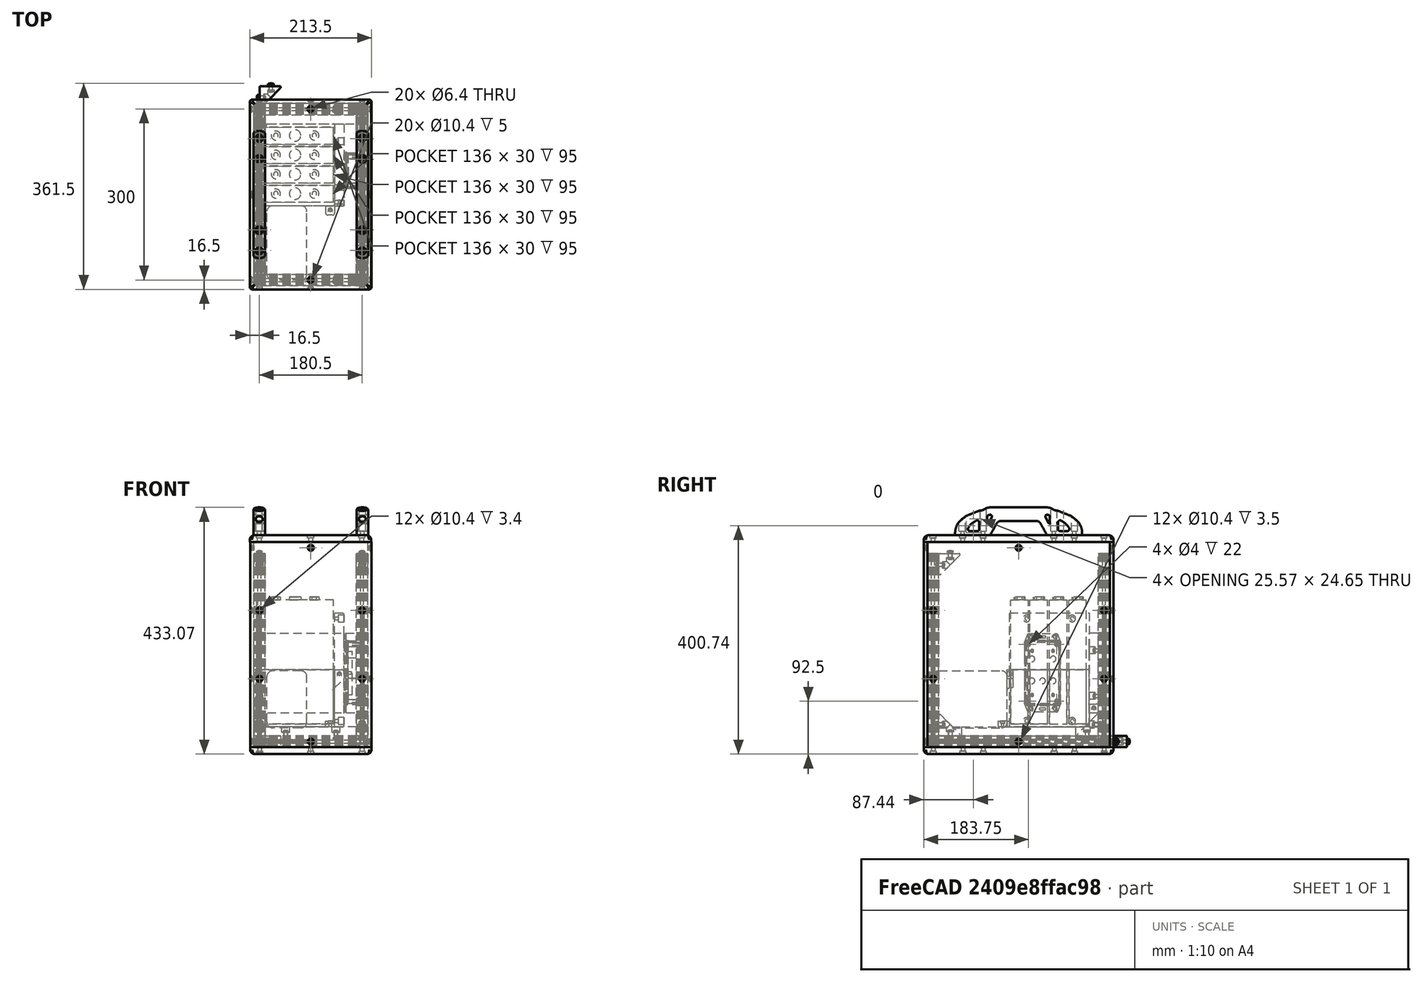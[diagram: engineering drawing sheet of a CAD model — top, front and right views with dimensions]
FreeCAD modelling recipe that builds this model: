
FCSTD DOCUMENT  (FreeCAD 0.17R9796 (Git))
Label: UPKframeNG2g
License: All rights reserved
LicenseURL: http://en.wikipedia.org/wiki/All_rights_reserved
objects: Part::Feature×72, Part::FeaturePython×24, Part::Compound×12, App::FeaturePython×8, App::Part×6, Part::Cylinder×5, Part::Box×4, Part::Cut×4, PartDesign::Body×2, PartDesign::Pocket×1, Part::Fillet×1, Part::MultiFuse×1
note: 127 computed .brp shape members not serialized (recipe doc carries the construction recipe); baked Part::Feature solids carry a one-line shape summary decoded from their .brp

FEATURE [Part::Feature] Pocket003001  label="tslot32con"
  Placement = pos=(0,10,10) rot=(1,0,0;1.5708rad)
  shape: bbox 20 x 320 x 20 mm, 150 faces (baked)
FEATURE [Part::Feature] Pocket003002  label="tslot16"
  Placement = pos=(10,0,10) rot=(0,1,0;1.5708rad)
  shape: bbox 160 x 20 x 20 mm, 94 faces (baked)
FEATURE [Part::Feature] Pocket003006  label="tslot16_001"
  Placement = pos=(10,-300,10) rot=(0,1,0;1.5708rad)
  shape: bbox 160 x 20 x 20 mm, 94 faces (baked)
FEATURE [Part::Feature] Pocket003007  label="tslot32con_001"
  Placement = pos=(180,-310,10) rot=(0,0.707107,0.707107;3.14159rad)
  shape: bbox 20 x 320 x 20 mm, 150 faces (baked)
FEATURE [Part::FeaturePython] Screw  label="M6x25-Screw"  # Fasteners workbench fastener (typed FeaturePython)
  Placement = pos=(-4,0,10) rot=(0,-1,0;1.5708rad)
  diameter = 7
  invert = false
  length = 6
  matchOuter = false
  offset = 0
  thread = false
  type = 15
FEATURE [Part::FeaturePython] Screw001  label="M6x25-Screw004"  # Fasteners workbench fastener (typed FeaturePython)
  Placement = pos=(-4,-300,10) rot=(0,-1,0;1.5708rad)
  diameter = 7
  invert = false
  length = 6
  matchOuter = false
  offset = 0
  thread = false
  type = 15
FEATURE [Part::FeaturePython] Screw002  label="M6x25-Screw005"  # Fasteners workbench fastener (typed FeaturePython)
  Placement = pos=(184,0,10) rot=(0,1,0;1.5708rad)
  diameter = 7
  invert = false
  length = 6
  matchOuter = false
  offset = 0
  thread = false
  type = 15
FEATURE [Part::FeaturePython] Screw004  label="M6x25-Screw006"  # Fasteners workbench fastener (typed FeaturePython)
  Placement = pos=(184,-300,10) rot=(0,1,0;1.5708rad)
  diameter = 7
  invert = false
  length = 6
  matchOuter = false
  offset = 0
  thread = false
  type = 15
FEATURE [App::Part] Part  label="lower_frame"
  Group = -> [Pocket003001,Pocket003002,Pocket003006,Pocket003007,Screw,Screw001,Screw002,Screw004]
  License = CC BY 3.0
  LicenseURL = http://creativecommons.org/licenses/by/3.0/
  Origin = -> PartOrigin
FEATURE [Part::Feature] Pocket003008  label="tslot32con001"
  Placement = pos=(0,10,10) rot=(1,0,0;1.5708rad)
  shape: bbox 20 x 320 x 20 mm, 150 faces (baked)
FEATURE [Part::Feature] Pocket003009  label="tslot041"
  Placement = pos=(10,0,10) rot=(0,1,0;1.5708rad)
  shape: bbox 160 x 20 x 20 mm, 94 faces (baked)
FEATURE [Part::Feature] Pocket003010  label="tslot16_002"
  Placement = pos=(10,-300,10) rot=(0,1,0;1.5708rad)
  shape: bbox 160 x 20 x 20 mm, 94 faces (baked)
FEATURE [Part::Feature] Pocket003011  label="tslot32con_002"
  Placement = pos=(180,-310,10) rot=(0,0.707107,0.707107;3.14159rad)
  shape: bbox 20 x 320 x 20 mm, 150 faces (baked)
FEATURE [Part::FeaturePython] Screw005  label="M6x25-Screw007"  # Fasteners workbench fastener (typed FeaturePython)
  Placement = pos=(-4,0,10) rot=(0,-1,0;1.5708rad)
  diameter = 7
  invert = false
  length = 6
  matchOuter = false
  offset = 0
  thread = false
  type = 15
FEATURE [Part::FeaturePython] Screw006  label="M6x25-Screw008"  # Fasteners workbench fastener (typed FeaturePython)
  Placement = pos=(-4,-300,10) rot=(0,-1,0;1.5708rad)
  diameter = 7
  invert = false
  length = 6
  matchOuter = false
  offset = 0
  thread = false
  type = 15
FEATURE [Part::FeaturePython] Screw007  label="M6x25-Screw009"  # Fasteners workbench fastener (typed FeaturePython)
  Placement = pos=(184,0,10) rot=(0,1,0;1.5708rad)
  diameter = 7
  invert = false
  length = 6
  matchOuter = false
  offset = 0
  thread = false
  type = 15
FEATURE [Part::FeaturePython] Screw008  label="M6x25-Screw010"  # Fasteners workbench fastener (typed FeaturePython)
  Placement = pos=(184,-300,10) rot=(0,1,0;1.5708rad)
  diameter = 7
  invert = false
  length = 6
  matchOuter = false
  offset = 0
  thread = false
  type = 15
FEATURE [App::Part] Part001  label="upper_frame"
  Group = -> [Pocket003008,Pocket003009,Pocket003010,Pocket003011,Screw005,Screw006,Screw007,Screw008]
  License = CC BY 3.0
  LicenseURL = http://creativecommons.org/licenses/by/3.0/
  Origin = -> PartOrigin001
  Placement = pos=(0,0,340) rot=(0,0,1;0rad)
FEATURE [Part::Feature] Fillet004001  label="Fillet005"
  shape: bbox 37.5 x 37.5 x 20 mm, 26 faces (baked)
FEATURE [Part::FeaturePython] Screw009  label="M6x12-Screw"  # Fasteners workbench fastener (typed FeaturePython)
  Placement = pos=(7,20,10) rot=(0,1,0;1.5708rad)
  diameter = 4
  invert = false
  length = 1
  matchOuter = false
  offset = 0
  thread = false
  type = 20
FEATURE [Part::Feature] Body001  label="m6nutplate"
  Placement = pos=(-1.5,15,5) rot=(0,-1,0;1.5708rad)
  shape: bbox 3 x 10 x 10 mm, 9 faces (baked)
FEATURE [App::Part] Part002  label="cornerstonescrewnut"
  License = CC BY 3.0
  LicenseURL = http://creativecommons.org/licenses/by/3.0/
  Origin = -> PartOrigin002
  Placement = pos=(10,-50,20) rot=(0,-1,0;1.5708rad)
FEATURE [Part::FeaturePython] Screw010  label="M6x12-Screw001"  # Fasteners workbench fastener (typed FeaturePython)
  Placement = pos=(20,33,10) rot=(1,0,0;1.5708rad)
  diameter = 4
  invert = false
  length = 1
  matchOuter = false
  offset = 0
  thread = false
  type = 20
FEATURE [Part::Feature] Body002  label="m6nutplate001"
  Placement = pos=(15,41.5,5) rot=(0.57735,0.57735,0.57735;4.18879rad)
  shape: bbox 10 x 3 x 10 mm, 9 faces (baked)
FEATURE [Part::Feature] Fillet004002  label="Fillet006"
  shape: bbox 37.5 x 37.5 x 20 mm, 26 faces (baked)
FEATURE [Part::FeaturePython] Screw011  label="M6x12-Screw002"  # Fasteners workbench fastener (typed FeaturePython)
  Placement = pos=(7,20,10) rot=(0,1,0;1.5708rad)
  diameter = 4
  invert = false
  length = 1
  matchOuter = false
  offset = 0
  thread = false
  type = 20
FEATURE [Part::Feature] Body003  label="m6nutplate002"
  Placement = pos=(-1.5,15,5) rot=(0,-1,0;1.5708rad)
  shape: bbox 3 x 10 x 10 mm, 9 faces (baked)
FEATURE [Part::FeaturePython] Screw012  label="M6x12-Screw003"  # Fasteners workbench fastener (typed FeaturePython)
  Placement = pos=(20,33,10) rot=(1,0,0;1.5708rad)
  diameter = 4
  invert = false
  length = 1
  matchOuter = false
  offset = 0
  thread = false
  type = 20
FEATURE [Part::Feature] Body004  label="m6nutplate003"
  Placement = pos=(15,41.5,5) rot=(0.57735,0.57735,0.57735;4.18879rad)
  shape: bbox 10 x 3 x 10 mm, 9 faces (baked)
FEATURE [App::Part] Part003  label="cornerstonescrewnut001"
  Group = -> [Body003,Screw011,Fillet004002,Screw012,Body004,PartOrigin002,Body001,Screw009,Fillet004001,Screw010,Body002,Part002]
  License = CC BY 3.0
  LicenseURL = http://creativecommons.org/licenses/by/3.0/
  Origin = -> PartOrigin003
  Placement = pos=(190,-50,20) rot=(0,-1,0;1.5708rad)
FEATURE [Part::Feature] Fillet004003  label="Fillet007"
  shape: bbox 37.5 x 37.5 x 20 mm, 26 faces (baked)
FEATURE [Part::FeaturePython] Screw013  label="M6x12-Screw004"  # Fasteners workbench fastener (typed FeaturePython)
  Placement = pos=(7,20,10) rot=(0,1,0;1.5708rad)
  diameter = 4
  invert = false
  length = 1
  matchOuter = false
  offset = 0
  thread = false
  type = 20
FEATURE [Part::Feature] Body005  label="m6nutplate004"
  Placement = pos=(-1.5,15,5) rot=(0,-1,0;1.5708rad)
  shape: bbox 3 x 10 x 10 mm, 9 faces (baked)
FEATURE [Part::FeaturePython] Screw014  label="M6x12-Screw005"  # Fasteners workbench fastener (typed FeaturePython)
  Placement = pos=(20,33,10) rot=(1,0,0;1.5708rad)
  diameter = 4
  invert = false
  length = 1
  matchOuter = false
  offset = 0
  thread = false
  type = 20
FEATURE [Part::Feature] Body006  label="m6nutplate005"
  Placement = pos=(15,41.5,5) rot=(0.57735,0.57735,0.57735;4.18879rad)
  shape: bbox 10 x 3 x 10 mm, 9 faces (baked)
FEATURE [App::Part] Part004  label="cornerstonescrewnut002"
  Group = -> [Body005,Screw013,Fillet004003,Screw014,Body006]
  License = CC BY 3.0
  LicenseURL = http://creativecommons.org/licenses/by/3.0/
  Origin = -> PartOrigin004
  Placement = pos=(-10,-50,340) rot=(0,1,0;1.5708rad)
FEATURE [Part::Feature] Fillet004004  label="Fillet008"
  shape: bbox 37.5 x 37.5 x 20 mm, 26 faces (baked)
FEATURE [Part::FeaturePython] Screw015  label="M6x12-Screw006"  # Fasteners workbench fastener (typed FeaturePython)
  Placement = pos=(7,20,10) rot=(0,1,0;1.5708rad)
  diameter = 4
  invert = false
  length = 1
  matchOuter = false
  offset = 0
  thread = false
  type = 20
FEATURE [Part::Feature] Body007  label="m6nutplate006"
  Placement = pos=(-1.5,15,5) rot=(0,-1,0;1.5708rad)
  shape: bbox 3 x 10 x 10 mm, 9 faces (baked)
FEATURE [Part::FeaturePython] Screw016  label="M6x12-Screw007"  # Fasteners workbench fastener (typed FeaturePython)
  Placement = pos=(20,33,10) rot=(1,0,0;1.5708rad)
  diameter = 4
  invert = false
  length = 1
  matchOuter = false
  offset = 0
  thread = false
  type = 20
FEATURE [Part::Feature] Body008  label="m6nutplate007"
  Placement = pos=(15,41.5,5) rot=(0.57735,0.57735,0.57735;4.18879rad)
  shape: bbox 10 x 3 x 10 mm, 9 faces (baked)
FEATURE [App::Part] Part005  label="cornerstonescrewnut003"
  Group = -> [Body007,Screw015,Fillet004004,Screw016,Body008]
  License = CC BY 3.0
  LicenseURL = http://creativecommons.org/licenses/by/3.0/
  Origin = -> PartOrigin005
  Placement = pos=(170,-50,340) rot=(0,1,0;1.5708rad)
FEATURE [Part::Feature] Body009001  label="m6nutplate010"
  Placement = pos=(-1.5,15,5) rot=(0,-1,0;1.5708rad)
  shape: bbox 3 x 10 x 10 mm, 9 faces (baked)
FEATURE [Part::Feature] Body010001  label="m6nutplate011"
  Placement = pos=(15,41.5,5) rot=(0.57735,0.57735,0.57735;4.18879rad)
  shape: bbox 10 x 3 x 10 mm, 9 faces (baked)
FEATURE [Part::Feature] Screw018001  label="M6x12-Screw010"
  Placement = pos=(20,33,10) rot=(1,0,0;1.5708rad)
  shape: bbox 10.5 x 15.3 x 10.5 mm, 15 faces (baked)
FEATURE [Part::Feature] Screw017001  label="M6x12-Screw011"
  Placement = pos=(7,20,10) rot=(0,1,0;1.5708rad)
  shape: bbox 15.3 x 10.5 x 10.5 mm, 15 faces (baked)
FEATURE [Part::Feature] Fillet004005001  label="Fillet010"
  shape: bbox 37.5 x 37.5 x 20 mm, 26 faces (baked)
FEATURE [Part::Compound] Compound
  Links = -> [Body009001,Fillet004005001,Screw017001,Body010001,Screw018001]
  Placement = pos=(10,-250,340) rot=(0.707107,0,-0.707107;3.14159rad)
FEATURE [Part::Feature] Body010002  label="m6nutplate012"
  Placement = pos=(-1.5,15,5) rot=(0,-1,0;1.5708rad)
  shape: bbox 3 x 10 x 10 mm, 9 faces (baked)
FEATURE [Part::Feature] Body010003  label="m6nutplate013"
  Placement = pos=(15,41.5,5) rot=(0.57735,0.57735,0.57735;4.18879rad)
  shape: bbox 10 x 3 x 10 mm, 9 faces (baked)
FEATURE [Part::Feature] Screw018002  label="M6x12-Screw012"
  Placement = pos=(20,33,10) rot=(1,0,0;1.5708rad)
  shape: bbox 10.5 x 15.3 x 10.5 mm, 15 faces (baked)
FEATURE [Part::Feature] Screw018003  label="M6x12-Screw013"
  Placement = pos=(7,20,10) rot=(0,1,0;1.5708rad)
  shape: bbox 15.3 x 10.5 x 10.5 mm, 15 faces (baked)
FEATURE [Part::Feature] Fillet004005002  label="Fillet011"
  shape: bbox 37.5 x 37.5 x 20 mm, 26 faces (baked)
FEATURE [Part::Compound] Compound001
  Links = -> [Body010002,Fillet004005002,Screw018003,Body010003,Screw018002]
  Placement = pos=(190,-250,340) rot=(0.707107,0,-0.707107;3.14159rad)
FEATURE [Part::Feature] Body010004  label="m6nutplate014"
  Placement = pos=(-1.5,15,5) rot=(0,-1,0;1.5708rad)
  shape: bbox 3 x 10 x 10 mm, 9 faces (baked)
FEATURE [Part::Feature] Body010005  label="m6nutplate015"
  Placement = pos=(15,41.5,5) rot=(0.57735,0.57735,0.57735;4.18879rad)
  shape: bbox 10 x 3 x 10 mm, 9 faces (baked)
FEATURE [Part::Feature] Screw018004  label="M6x12-Screw014"
  Placement = pos=(20,33,10) rot=(1,0,0;1.5708rad)
  shape: bbox 10.5 x 15.3 x 10.5 mm, 15 faces (baked)
FEATURE [Part::Feature] Screw018005  label="M6x12-Screw015"
  Placement = pos=(7,20,10) rot=(0,1,0;1.5708rad)
  shape: bbox 15.3 x 10.5 x 10.5 mm, 15 faces (baked)
FEATURE [Part::Feature] Fillet004005003  label="Fillet012"
  shape: bbox 37.5 x 37.5 x 20 mm, 26 faces (baked)
FEATURE [Part::Compound] Compound002
  Links = -> [Body010004,Fillet004005003,Screw018005,Body010005,Screw018004]
  Placement = pos=(10,-290,60) rot=(0.57735,0.57735,-0.57735;4.18879rad)
FEATURE [Part::Feature] Body010006  label="m6nutplate016"
  Placement = pos=(-1.5,15,5) rot=(0,-1,0;1.5708rad)
  shape: bbox 3 x 10 x 10 mm, 9 faces (baked)
FEATURE [Part::Feature] Body010007  label="m6nutplate017"
  Placement = pos=(15,41.5,5) rot=(0.57735,0.57735,0.57735;4.18879rad)
  shape: bbox 10 x 3 x 10 mm, 9 faces (baked)
FEATURE [Part::Feature] Screw018006  label="M6x12-Screw016"
  Placement = pos=(20,33,10) rot=(1,0,0;1.5708rad)
  shape: bbox 10.5 x 15.3 x 10.5 mm, 15 faces (baked)
FEATURE [Part::Feature] Screw018007  label="M6x12-Screw017"
  Placement = pos=(7,20,10) rot=(0,1,0;1.5708rad)
  shape: bbox 15.3 x 10.5 x 10.5 mm, 15 faces (baked)
FEATURE [Part::Feature] Fillet004005004  label="Fillet013"
  shape: bbox 37.5 x 37.5 x 20 mm, 26 faces (baked)
FEATURE [Part::Compound] Compound003
  Links = -> [Body010006,Fillet004005004,Screw018007,Body010007,Screw018006]
  Placement = pos=(190,-290,60) rot=(0.57735,0.57735,-0.57735;4.18879rad)
FEATURE [Part::Feature] Pocket001001  label="tslot32"
  Placement = pos=(0,0,20) rot=(0,0,1;0rad)
  shape: bbox 20 x 20 x 320 mm, 94 faces (baked)
FEATURE [Part::Feature] Body010008  label="m6nutplate018"
  Placement = pos=(-1.5,15,5) rot=(0,-1,0;1.5708rad)
  shape: bbox 3 x 10 x 10 mm, 9 faces (baked)
FEATURE [Part::Feature] Body010009  label="m6nutplate019"
  Placement = pos=(15,41.5,5) rot=(0.57735,0.57735,0.57735;4.18879rad)
  shape: bbox 10 x 3 x 10 mm, 9 faces (baked)
FEATURE [Part::Feature] Screw018008  label="M6x12-Screw018"
  Placement = pos=(20,33,10) rot=(1,0,0;1.5708rad)
  shape: bbox 10.5 x 15.3 x 10.5 mm, 15 faces (baked)
FEATURE [Part::Feature] Screw018009  label="M6x12-Screw019"
  Placement = pos=(7,20,10) rot=(0,1,0;1.5708rad)
  shape: bbox 15.3 x 10.5 x 10.5 mm, 15 faces (baked)
FEATURE [Part::Feature] Fillet004005005  label="Fillet014"
  shape: bbox 37.5 x 37.5 x 20 mm, 26 faces (baked)
FEATURE [Part::Compound] Compound004
  Links = -> [Body010008,Fillet004005005,Screw018009,Body010009,Screw018008]
  Placement = pos=(-10,-10,60) rot=(0.57735,-0.57735,0.57735;4.18879rad)
FEATURE [Part::Feature] Pocket003012  label="tslot32_001"
  Placement = pos=(0,-300,20) rot=(0,0,1;0rad)
  shape: bbox 20 x 20 x 320 mm, 94 faces (baked)
FEATURE [Part::Feature] Pocket003013  label="tslot32_002"
  Placement = pos=(180,0,20) rot=(0,0,1;0rad)
  shape: bbox 20 x 20 x 320 mm, 94 faces (baked)
FEATURE [Part::Feature] Pocket003014  label="tslot32_003"
  Placement = pos=(180,-300,20) rot=(0,0,1;0rad)
  shape: bbox 20 x 20 x 320 mm, 94 faces (baked)
FEATURE [PartDesign::Body] Body010027
FEATURE [Part::FeaturePython] Screw018021  label="M6x12-Screw032"  # Fasteners workbench fastener (typed FeaturePython)
  diameter = 4
  invert = false
  length = 1
  matchOuter = false
  offset = 0
  thread = false
  type = 20
FEATURE [Part::Feature] Body010028  label="m6nutplate032"
  Placement = pos=(5,-5,-8.39) rot=(0,1,0;3.14159rad)
  shape: bbox 10 x 10 x 3 mm, 9 faces (baked)
FEATURE [App::FeaturePython] circularEdgeConstraint009  # a2plus constraint (typed FeaturePython)
  Object1 = Screw
  Object2 = Body001
  SubElement1 = Edge7
  SubElement2 = Edge20
  Type = circularEdge
  directionConstraint = 1
  lockRotation = false
  offset = 0
FEATURE [Part::Compound] Compound017  label="nutplate12screw008"
  Links = -> [Screw018021,circularEdgeConstraint009,Body010028]
  Placement = pos=(10,30,6) rot=(0,0,1;0rad)
FEATURE [Part::FeaturePython] Screw018022  label="M6x12-Screw033"  # Fasteners workbench fastener (typed FeaturePython)
  diameter = 4
  invert = false
  length = 1
  matchOuter = false
  offset = 0
  thread = false
  type = 20
FEATURE [Part::Feature] Body010029  label="m6nutplate033"
  Placement = pos=(5,-5,-8.39) rot=(0,1,0;3.14159rad)
  shape: bbox 10 x 10 x 3 mm, 9 faces (baked)
FEATURE [App::FeaturePython] circularEdgeConstraint010  # a2plus constraint (typed FeaturePython)
  Object1 = Screw
  Object2 = Body001
  SubElement1 = Edge7
  SubElement2 = Edge20
  Type = circularEdge
  directionConstraint = 1
  lockRotation = false
  offset = 0
FEATURE [Part::Compound] Compound018  label="nutplate12screw009"
  Links = -> [Screw018022,circularEdgeConstraint010,Body010029]
  Placement = pos=(10,110,6) rot=(0,0,1;0rad)
FEATURE [Part::FeaturePython] Screw018023  label="M6x12-Screw034"  # Fasteners workbench fastener (typed FeaturePython)
  diameter = 4
  invert = false
  length = 1
  matchOuter = false
  offset = 0
  thread = false
  type = 20
FEATURE [Part::Feature] Body010030  label="m6nutplate034"
  Placement = pos=(5,-5,-8.39) rot=(0,1,0;3.14159rad)
  shape: bbox 10 x 10 x 3 mm, 9 faces (baked)
FEATURE [App::FeaturePython] circularEdgeConstraint011  # a2plus constraint (typed FeaturePython)
  Object1 = Screw
  Object2 = Body001
  SubElement1 = Edge7
  SubElement2 = Edge20
  Type = circularEdge
  directionConstraint = 1
  lockRotation = false
  offset = 0
FEATURE [Part::Compound] Compound019  label="nutplate12screw010"
  Links = -> [Screw018023,circularEdgeConstraint011,Body010030]
  Placement = pos=(190,110,6) rot=(0,0,1;0rad)
FEATURE [Part::FeaturePython] Screw018024  label="M6x12-Screw035"  # Fasteners workbench fastener (typed FeaturePython)
  diameter = 4
  invert = false
  length = 1
  matchOuter = false
  offset = 0
  thread = false
  type = 20
FEATURE [Part::Feature] Body010031  label="m6nutplate035"
  Placement = pos=(5,-5,-8.39) rot=(0,1,0;3.14159rad)
  shape: bbox 10 x 10 x 3 mm, 9 faces (baked)
FEATURE [App::FeaturePython] circularEdgeConstraint012  # a2plus constraint (typed FeaturePython)
  Object1 = Screw
  Object2 = Body001
  SubElement1 = Edge7
  SubElement2 = Edge20
  Type = circularEdge
  directionConstraint = 1
  lockRotation = false
  offset = 0
FEATURE [Part::Compound] Compound020  label="nutplate12screw011"
  Links = -> [Screw018024,circularEdgeConstraint012,Body010031]
  Placement = pos=(190,30,6) rot=(0,0,1;0rad)
FEATURE [Part::Compound] Compound021  label="front_plate"
  Links = -> [Body010027,Compound020,Compound019,Compound017,Compound018]
  Placement = pos=(-10,-10,60) rot=(1,0,0;1.5708rad)
FEATURE [Part::Compound] Compound016  label="bottom_plate"
  Placement = pos=(190,-310,20) rot=(0,0,1;1.5708rad)
FEATURE [PartDesign::Pocket] Pocket003019
  Length = 10
  Placement = pos=(130,-166,235) rot=(0,1,0;1.5708rad)
  Type = 0
FEATURE [Part::Box] Box003  label="MPPT"
  AttacherType = Attacher::AttachEngine3D
  Height = 100
  Length = 130
  Placement = pos=(290,128,10) rot=(0,0,1;0rad)
  Width = 70
FEATURE [Part::Fillet] Fillet007  label="MPPT               "
  Base = -> Box003
  Edges = 12 edges r=10: [Edge1,Edge2,Edge3,Edge4,Edge5,Edge6,Edge7,Edge8,Edge9,Edge10,Edge11,Edge12]
  Placement = pos=(211,-590,24) rot=(0,0,1;1.5708rad)
FEATURE [Part::Feature] Part__Feature1213  label="1591XXBF LID"
  Placement = pos=(153,-86,180) rot=(-0.57735,0.57735,0.57735;4.18879rad)
  shape: bbox 12.61 x 63.32 x 138 mm, 220 faces (baked)
FEATURE [Part::Feature] Part__Feature1212  label="1591XXB BOX"
  Placement = pos=(0,0,0) rot=(0,0.707107,0.707107;3.14159rad)
  shape: bbox 113.8 x 28.25 x 63.32 mm, 133 faces (baked)
FEATURE [Part::Cylinder] Cylinder  label="Zylinder"
  Angle = 360
  AttacherType = Attacher::AttachEngine3D
  Height = 60
  Placement = pos=(-14,48,18.6) rot=(1,0,0;1.5708rad)
  Radius = 5
FEATURE [Part::Cylinder] Cylinder001  label="Zylinder001"
  Angle = 360
  AttacherType = Attacher::AttachEngine3D
  Height = 60
  Placement = pos=(-14,48,0) rot=(1,0,0;1.5708rad)
  Radius = 5
FEATURE [Part::Cylinder] Cylinder002  label="Zylinder002"
  Angle = 360
  AttacherType = Attacher::AttachEngine3D
  Height = 60
  Placement = pos=(-14,48,-18.66) rot=(1,0,0;1.5708rad)
  Radius = 5
FEATURE [Part::Cylinder] Cylinder003  label="Zylinder003"
  Angle = 360
  AttacherType = Attacher::AttachEngine3D
  Height = 60
  Placement = pos=(24.49,48,18.6) rot=(1,0,0;1.5708rad)
  Radius = 5
FEATURE [Part::Cylinder] Cylinder004  label="Zylinder004"
  Angle = 360
  AttacherType = Attacher::AttachEngine3D
  Height = 60
  Placement = pos=(24.49,48,-18.66) rot=(1,0,0;1.5708rad)
  Radius = 5
FEATURE [Part::MultiFuse] Fusion
  Shapes = -> [Cylinder,Cylinder004,Cylinder003,Cylinder002,Cylinder001]
FEATURE [Part::Cut] Cut
  Base = -> Part__Feature1212
  Tool = -> Fusion
FEATURE [Part::Box] Box002  label="Würfel002"
  AttacherType = Attacher::AttachEngine3D
  Height = 10
  Length = 76
  Placement = pos=(-38,16,-36) rot=(0,0,1;0rad)
  Width = 12.6
FEATURE [Part::Cut] Cut001
  Base = -> Cut
  Tool = -> Box002
FEATURE [Part::Box] Box004  label="Würfel003"
  AttacherType = Attacher::AttachEngine3D
  Height = 10
  Length = 36
  Placement = pos=(-10,9,24) rot=(0,0,1;0rad)
  Width = 20
FEATURE [Part::Cut] Cut002
  Base = -> Cut001
  Tool = -> Box004
FEATURE [Part::Box] Box  label="Würfel"
  AttacherType = Attacher::AttachEngine3D
  Height = 20
  Length = 10
  Placement = pos=(49,23,-6) rot=(0,0,1;0rad)
  Width = 6
FEATURE [Part::Cut] Cut003  label="bms-cover"
  Base = -> Cut002
  Placement = pos=(179,-108,130.5) rot=(0.57735,-0.57735,0.57735;2.0944rad)
  Tool = -> Box
FEATURE [PartDesign::Body] Body010032
FEATURE [Part::FeaturePython] Screw018025  label="M6x12-Screw036"  # Fasteners workbench fastener (typed FeaturePython)
  diameter = 4
  invert = false
  length = 1
  matchOuter = false
  offset = 0
  thread = false
  type = 20
FEATURE [App::FeaturePython] circularEdgeConstraint013  # a2plus constraint (typed FeaturePython)
  Object1 = Screw
  Object2 = Body001
  SubElement1 = Edge7
  SubElement2 = Edge20
  Type = circularEdge
  directionConstraint = 1
  lockRotation = false
  offset = 0
FEATURE [Part::FeaturePython] Screw018026  label="M6x12-Screw037"  # Fasteners workbench fastener (typed FeaturePython)
  diameter = 4
  invert = false
  length = 1
  matchOuter = false
  offset = 0
  thread = false
  type = 20
FEATURE [Part::Feature] Body010034  label="m6nutplate037"
  Placement = pos=(5,-5,-8.39) rot=(0,1,0;3.14159rad)
  shape: bbox 10 x 10 x 3 mm, 9 faces (baked)
FEATURE [App::FeaturePython] circularEdgeConstraint014  # a2plus constraint (typed FeaturePython)
  Object1 = Screw
  Object2 = Body001
  SubElement1 = Edge7
  SubElement2 = Edge20
  Type = circularEdge
  directionConstraint = 1
  lockRotation = false
  offset = 0
FEATURE [Part::FeaturePython] Screw018027  label="M6x12-Screw038"  # Fasteners workbench fastener (typed FeaturePython)
  diameter = 4
  invert = false
  length = 1
  matchOuter = false
  offset = 0
  thread = false
  type = 20
FEATURE [Part::Feature] Body010035  label="m6nutplate038"
  Placement = pos=(5,-5,-8.39) rot=(0,1,0;3.14159rad)
  shape: bbox 10 x 10 x 3 mm, 9 faces (baked)
FEATURE [App::FeaturePython] circularEdgeConstraint015  # a2plus constraint (typed FeaturePython)
  Object1 = Screw
  Object2 = Body001
  SubElement1 = Edge7
  SubElement2 = Edge20
  Type = circularEdge
  directionConstraint = 1
  lockRotation = false
  offset = 0
FEATURE [Part::FeaturePython] Screw018028  label="M6x12-Screw039"  # Fasteners workbench fastener (typed FeaturePython)
  diameter = 4
  invert = false
  length = 1
  matchOuter = false
  offset = 0
  thread = false
  type = 20
FEATURE [Part::Feature] Body010036  label="m6nutplate039"
  Placement = pos=(5,-5,-8.39) rot=(0,1,0;3.14159rad)
  shape: bbox 10 x 10 x 3 mm, 9 faces (baked)
FEATURE [App::FeaturePython] circularEdgeConstraint016  # a2plus constraint (typed FeaturePython)
  Object1 = Screw
  Object2 = Body001
  SubElement1 = Edge7
  SubElement2 = Edge20
  Type = circularEdge
  directionConstraint = 1
  lockRotation = false
  offset = 0
FEATURE [Part::Compound] Compound026  label="bmsmounting_plate"
  Links = -> [Body010032]
  Placement = pos=(132,-26,36) rot=(0.707107,0,0.707107;3.14159rad)
FEATURE [Part::Feature] Body010037  label="batterymount"
  Placement = pos=(-10,-170,36) rot=(0,0,1;0rad)
  shape: bbox 158 x 176 x 100 mm, 72 faces (baked)
FEATURE [Part::Feature] Body010033  label="m6nutplate036"
  Placement = pos=(5,-5,-8.39) rot=(0,1,0;3.14159rad)
  shape: bbox 10 x 10 x 3 mm, 9 faces (baked)
FEATURE [Part::Feature] Body010038  label="cam72"
  Placement = pos=(130,-62,41) rot=(0,0,1;1.5708rad)
  shape: bbox 135.1 x 31 x 222.5 mm, 16 faces (baked)
FEATURE [Part::Feature] Body010039  label="cam72_001"
  Placement = pos=(130,-96,41) rot=(0,0,1;1.5708rad)
  shape: bbox 135.1 x 31 x 222.5 mm, 16 faces (baked)
FEATURE [Part::Feature] Body010040  label="cam72_002"
  Placement = pos=(130,-130,41) rot=(0,0,1;1.5708rad)
  shape: bbox 135.1 x 31 x 222.5 mm, 16 faces (baked)
FEATURE [Part::Feature] Body010041  label="cam72_003"
  Placement = pos=(130,-164,41) rot=(0,0,1;1.5708rad)
  shape: bbox 135.1 x 31 x 222.5 mm, 16 faces (baked)
FEATURE [Part::Feature] Body010042  label="backCover"
  Placement = pos=(-16.5,-310,0) rot=(1,0,0;1.5708rad)
  shape: bbox 213 x 6.5 x 360 mm, 26 faces (baked)
FEATURE [Part::Feature] Body010043  label="frontCover"
  Placement = pos=(196.5,10,0) rot=(0,0.707107,0.707107;3.14159rad)
  shape: bbox 213 x 6.5 x 360 mm, 26 faces (baked)
FEATURE [Part::Feature] Body010044  label="topCover"
  Placement = pos=(-17,-316.5,360) rot=(0,0,1;0rad)
  shape: bbox 213 x 333 x 12 mm, 48 faces (baked)
FEATURE [Part::Feature] Body010045  label="bottomCover"
  Placement = pos=(196.5,-316.5,0) rot=(0,1,0;3.14159rad)
  shape: bbox 213 x 333 x 12 mm, 48 faces (baked)
FEATURE [Part::Feature] Pocket003020  label="sideCover"
  Placement = pos=(190,-310,0) rot=(0.57735,0.57735,0.57735;2.0944rad)
  shape: bbox 6.5 x 320 x 360 mm, 24 faces (baked)
FEATURE [Part::Feature] Pocket003021  label="sideCover001"
  Placement = pos=(-10,10,0) rot=(-0.57735,0.57735,0.57735;4.18879rad)
  shape: bbox 6.5 x 320 x 360 mm, 24 faces (baked)
FEATURE [Part::Feature] Cut007001  label="handle"
  Placement = pos=(7,-150,372) rot=(0.57735,-0.57735,-0.57735;2.0944rad)
  shape: bbox 20 x 223 x 50.93 mm, 233 faces (baked)
FEATURE [Part::Feature] Cut007002  label="handle001"
  Placement = pos=(188,-150,372) rot=(0.57735,-0.57735,-0.57735;2.0944rad)
  shape: bbox 20 x 223 x 50.93 mm, 233 faces (baked)
